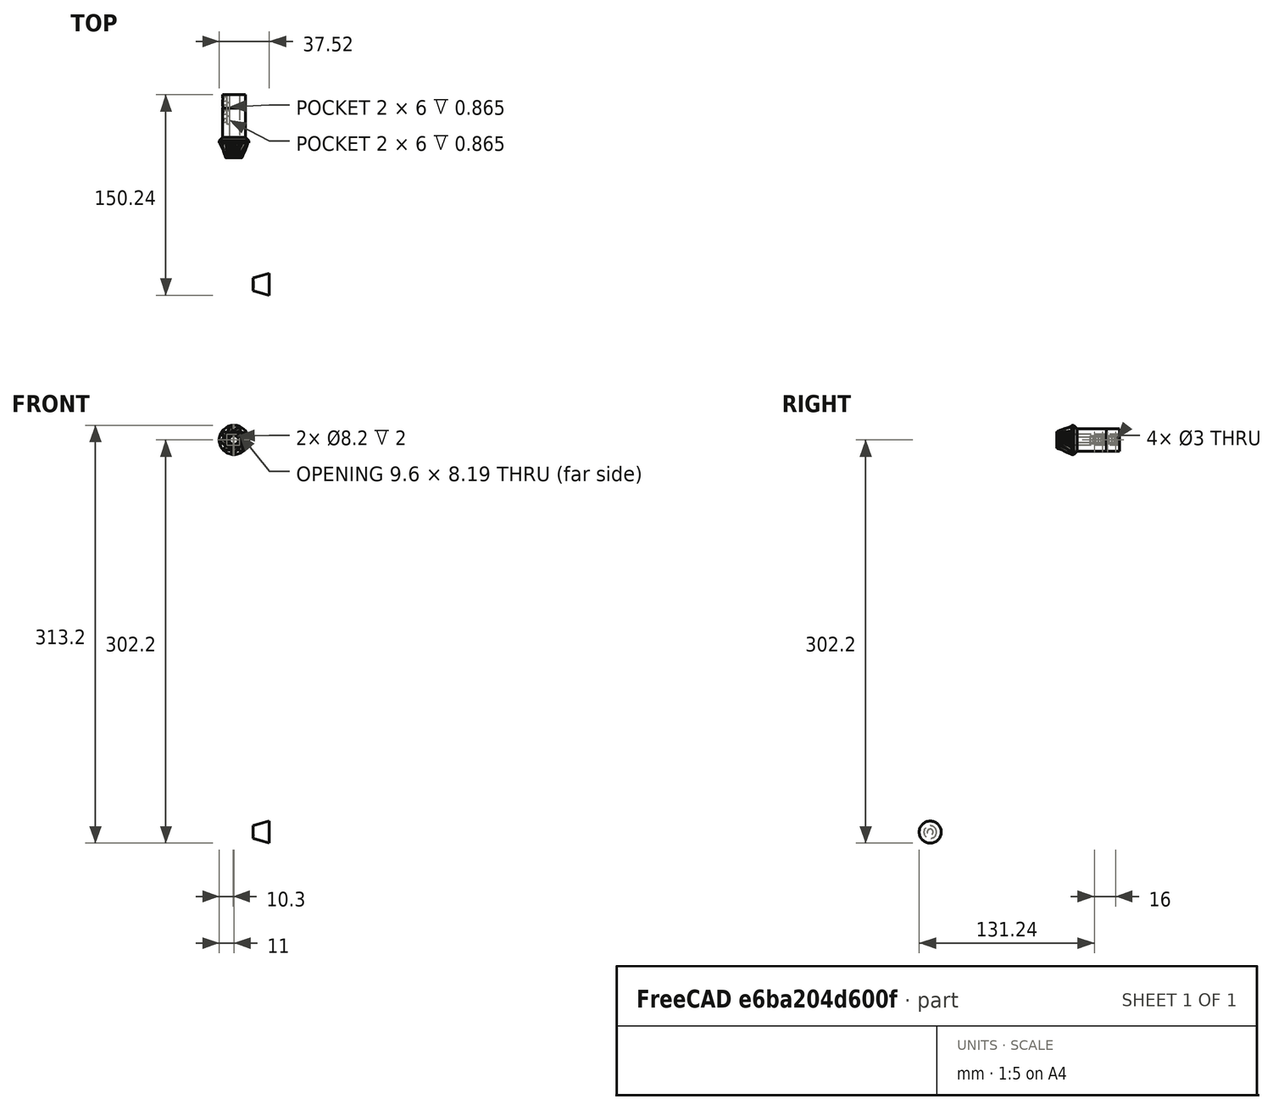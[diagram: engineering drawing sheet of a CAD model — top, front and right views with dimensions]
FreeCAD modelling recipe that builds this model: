
FCSTD DOCUMENT  (FreeCAD 0.19R24291 (Git))
Label: bazovina-prevod-C_007
License: All rights reserved
LicenseURL: http://en.wikipedia.org/wiki/All_rights_reserved
objects: Part::Cut×12, Part::Box×10, Part::Cylinder×9, Part::Compound×7, Part::FeaturePython×4, Sketcher::SketchObject×4, PartDesign::Revolution×4, PartDesign::Body×4, Part::Common×2, Part::MultiFuse×2, Mesh::Feature×2, Part::Chamfer×1
note: 63 computed .brp shape members not serialized (recipe doc carries the construction recipe); baked Part::Feature solids carry a one-line shape summary decoded from their .brp

FEATURE [Part::FeaturePython] bevelgear007  # WARN: FeaturePython — macro-defined, semantics opaque (R4)
  AttacherType = Attacher::AttachEngine3D
  Placement = pos=(26,0,-244) rot=(0,-1,0;1.5708rad)
  backlash = 0.1
  beta = 12
  clearance = 0.1
  height = 25
  module = 1.5
  numpoints = 6
  pitch_angle = 12.53
  pressure_angle = 25
  reset_origin = true
  teeth = 8
  version = 0.0.3
FEATURE [Sketcher::SketchObject] Sketch007
  FullyConstrained = false
  MapMode = 5
  Placement = pos=(0,0,0) rot=(1,0,0;1.5708rad)
  Support = -> [XZ_Plane007]
  sketch-geometry (31):
    g0: LineSegment StartX=0 StartY=-49.2912 StartZ=0 EndX=22.5 EndY=-49.2912 EndZ=0
    g1: LineSegment StartX=22.5 StartY=-49.2912 StartZ=0 EndX=22.5 EndY=-53.2912 EndZ=0
    g2: LineSegment StartX=22.5 StartY=-53.2912 StartZ=0 EndX=0 EndY=-53.2912 EndZ=0
    g3: LineSegment StartX=0 StartY=-53.2912 StartZ=0 EndX=0 EndY=-49.2912 EndZ=0
    g4: LineSegment StartX=22.5 StartY=-49.2912 StartZ=0 EndX=26.5 EndY=-49.2912 EndZ=0
    g5: LineSegment StartX=26.5 StartY=-49.2912 StartZ=0 EndX=26.5 EndY=-44.2912 EndZ=0
    g6: LineSegment StartX=26.5 StartY=-44.2912 StartZ=0 EndX=22.5 EndY=-44.2912 EndZ=0
    g7: LineSegment StartX=22.5 StartY=-44.2912 StartZ=0 EndX=22.5 EndY=-49.2912 EndZ=0
    g8: LineSegment StartX=22.5 StartY=-49.2912 StartZ=0 EndX=0 EndY=-49.2912 EndZ=0
    g9: LineSegment StartX=0 StartY=-49.2912 StartZ=0 EndX=0 EndY=-44.2912 EndZ=0
    g10: LineSegment StartX=0 StartY=-44.2912 StartZ=0 EndX=22.5 EndY=-44.2912 EndZ=0
    g11: LineSegment StartX=22.5 StartY=-44.2912 StartZ=0 EndX=22.5 EndY=-49.2912 EndZ=0
    g12: LineSegment StartX=0 StartY=-44.2912 StartZ=0 EndX=22.5 EndY=-49.2912 EndZ=0
    g13: LineSegment StartX=22.5 StartY=-49.2912 StartZ=0 EndX=22.0661 EndY=-51.2436 EndZ=0
    g14: LineSegment StartX=22.5 StartY=-49.2912 StartZ=0 EndX=22.9339 EndY=-47.3388 EndZ=0
    g15: LineSegment StartX=22.9339 StartY=-47.3388 StartZ=0 EndX=0 EndY=-44.2912 EndZ=0
    g16: LineSegment StartX=22.0661 StartY=-51.2436 StartZ=0 EndX=0 EndY=-44.2912 EndZ=0
    g17: LineSegment StartX=22.9339 StartY=-47.3388 StartZ=0 EndX=15.0036 EndY=-46.285 EndZ=0
    g18: LineSegment StartX=15.0036 StartY=-46.285 StartZ=0 EndX=14.3355 EndY=-49.2912 EndZ=0
    g19: LineSegment StartX=15.0036 StartY=-44.2912 StartZ=0 EndX=15.0036 EndY=-46.285 EndZ=0
    g20: LineSegment StartX=22.0661 StartY=-51.2436 StartZ=0 EndX=22.0661 EndY=-53.2912 EndZ=0
    g21: LineSegment StartX=22.9339 StartY=-47.3388 StartZ=0 EndX=26.5 EndY=-47.3388 EndZ=0
    g22: LineSegment StartX=15.0036 StartY=-44.2912 StartZ=0 EndX=15.0036 EndY=-46.5552 EndZ=0
    g23: LineSegment StartX=15.0036 StartY=-46.5552 StartZ=0 EndX=14.3773 EndY=-49.1034 EndZ=0
    g24: LineSegment StartX=14.3773 StartY=-49.1034 StartZ=0 EndX=22.0661 EndY=-51.2436 EndZ=0
    g25: LineSegment StartX=22.0661 StartY=-51.2436 StartZ=0 EndX=22.5 EndY=-49.2912 EndZ=0
    g26: LineSegment StartX=22.5 StartY=-49.2912 StartZ=0 EndX=26.5 EndY=-49.2912 EndZ=0
    g27: LineSegment StartX=26.5 StartY=-49.2912 StartZ=0 EndX=26.5 EndY=-44.2912 EndZ=0
    g28: LineSegment StartX=26.5 StartY=-44.2912 StartZ=0 EndX=15.0036 EndY=-44.2912 EndZ=0
    g29: LineSegment StartX=22.0661 StartY=-51.2436 StartZ=0 EndX=25.8788 EndY=-52.4534 EndZ=0
    g30: LineSegment StartX=25.8788 StartY=-52.4534 StartZ=0 EndX=26.5 EndY=-49.2912 EndZ=0
  constraints (81):
    c: Coincident(g0,g1)
    c: Coincident(g1,g2)
    c: Coincident(g2,g3)
    c: Coincident(g3,g0)
    c: Horizontal(g0)
    c: Horizontal(g2)
    c: Vertical(g1)
    c: Vertical(g3)
    c: PointOnObject(g0,g-2)
    c: Distance(g0) = 22.5
    c: Distance(g1) = 4
    c: Coincident(g4,g5)
    c: Coincident(g5,g6)
    c: Coincident(g6,g7)
    c: Coincident(g7,g4)
    c: Horizontal(g4)
    c: Horizontal(g6)
    c: Vertical(g5)
    c: Vertical(g7)
    c: Coincident(g4,g0)
    c: Distance(g7) = 5
    c: Distance(g6) = 4
    c: Coincident(g8,g9)
    c: Coincident(g9,g10)
    c: Coincident(g10,g11)
    c: Coincident(g11,g8)
    c: Horizontal(g8)
    c: Horizontal(g10)
    c: Vertical(g9)
    c: Vertical(g11)
    c: Coincident(g8,g0)
    c: PointOnObject(g9,g-2)
    c: Distance(g9) = 5
    c: Coincident(g12,g9)
    c: Coincident(g12,g0)
    c: Coincident(g13,g0)
    c: Perpendicular(g13,g12)
    c: Distance(g13) = 2
    c: Coincident(g14,g0)
    c: Distance(g14) = 2
    c: Perpendicular(g14,g12)
    c: Coincident(g15,g14)
    c: Coincident(g15,g9)
    c: Coincident(g16,g13)
    c: Coincident(g16,g9)
    c: Coincident(g17,g14)
    c: PointOnObject(g17,g15)
    c: Distance(g17) = 8
    c: Coincident(g18,g17)
    c: PointOnObject(g18,g0)
    c: Perpendicular(g18,g12)
    c: PointOnObject(g19,g10)
    c: Coincident(g19,g17)
    c: Vertical(g19)
    c: Coincident(g20,g13)
    c: PointOnObject(g20,g2)
    c: Vertical(g20)
    c: Coincident(g21,g14)
    c: PointOnObject(g21,g5)
    c: Horizontal(g21)
    c: Coincident(g19,g22)
    c: Coincident(g23,g22)
    c: PointOnObject(g23,g18)
    c: Coincident(g24,g23)
    c: Coincident(g24,g13)
    c: Coincident(g25,g24)
    c: Coincident(g25,g0)
    c: Coincident(g26,g25)
    c: Coincident(g26,g4)
    c: Coincident(g27,g26)
    c: Coincident(g27,g5)
    c: Coincident(g28,g27)
    c: Coincident(g28,g22)
    c: Vertical(g22)
    c: Angle(g15,g10) = 0.132114
    c: Angle(g12,g10) = 0.218669
    c: Angle(g9,g12) = 1.35213
    c: Coincident(g29,g24)
    c: Distance(g29) = 4
    c: Coincident(g30,g29)
    c: Coincident(g30,g26)
FEATURE [PartDesign::Revolution] Revolution007
  Angle = 360
  Axis = (22.5,0,0)
  Base = (0,9.8e-15,-44.2912)
  Placement = pos=(0,0,0) rot=(1,0,0;1.5708rad)
  Profile = -> Sketch007
  ReferenceAxis = -> Sketch007 [Axis10]
  Reversed = true
FEATURE [PartDesign::Body] Body007
  Group = -> [Sketch007,Revolution007]
  Origin = -> Origin007
  Placement = pos=(0,0,-199.6) rot=(0,0,1;0rad)
  Tip = -> Revolution007
FEATURE [Part::Common] Common009
  Base = -> Body007
  Placement = pos=(0,84,294) rot=(0,0,1;1.5708rad)
  Tool = -> bevelgear007
FEATURE [Part::Compound] Compound  label="bazovina-prevod-C1"
  Links = -> [Common009]
  Placement = pos=(0,-2,0) rot=(0,0,1;0rad)
FEATURE [Part::Box] Box247  label="Krychle247"
  AttacherType = Attacher::AttachEngine3D
  Height = 40
  Length = 40
  Placement = pos=(-20,98,30) rot=(0,0,1;0rad)
  Width = 20
FEATURE [Part::Box] Box248  label="Krychle248"
  AttacherType = Attacher::AttachEngine3D
  Height = 40
  Length = 40
  Placement = pos=(-20,88,30) rot=(0,0,1;0rad)
  Width = 20
FEATURE [Part::Box] Box249  label="Krychle249"
  AttacherType = Attacher::AttachEngine3D
  Height = 6
  Length = 6
  Placement = pos=(196.5,-3,18) rot=(0,0,1;1.5708rad)
  Width = 2
FEATURE [Part::Box] Box250  label="Krychle250"
  AttacherType = Attacher::AttachEngine3D
  Height = 6
  Length = 6
  Placement = pos=(196.5,-3,12) rot=(0,0,1;1.5708rad)
  Width = 2
FEATURE [Part::Compound] Compound027
  Links = -> [Box249,Box250]
  Placement = pos=(0,0,-20) rot=(0,0,1;0rad)
FEATURE [Part::Cylinder] Cylinder651  label="Válec651"
  Angle = 360
  AttacherType = Attacher::AttachEngine3D
  Height = 100
  Placement = pos=(100,0,21) rot=(0.57735,0.57735,0.57735;2.0944rad)
  Radius = 1.5
FEATURE [Part::Cylinder] Cylinder652  label="Válec652"
  Angle = 360
  AttacherType = Attacher::AttachEngine3D
  Height = 100
  Placement = pos=(100,0,15) rot=(0.57735,0.57735,0.57735;2.0944rad)
  Radius = 1.5
FEATURE [Part::Compound] Compound028
  Links = -> [Cylinder651,Cylinder652]
  Placement = pos=(0,0,-20) rot=(0,0,1;0rad)
FEATURE [Part::Box] Box251  label="Krychle251"
  AttacherType = Attacher::AttachEngine3D
  Height = 26
  Length = 2
  Placement = pos=(194.5,-4,4) rot=(0,0,1;0rad)
  Width = 8
FEATURE [Part::FeaturePython] Tube006  # WARN: FeaturePython — macro-defined, semantics opaque (R4)
  AttacherType = Attacher::AttachEngine3D
  Height = 32
  InnerRadius = 4.1
  OuterRadius = 8.5
  Placement = pos=(200,0,-8) rot=(0,0,1;0rad)
FEATURE [Part::MultiFuse] Fusion002
  Shapes = -> [Tube006,Box251]
FEATURE [Part::Cut] Cut257
  Base = -> Fusion002
  Tool = -> Compound027
FEATURE [Part::Cut] Cut259  label="super_spojka002"
  Base = -> Cut257
  Placement = pos=(-200,132,50) rot=(1,0,0;1.5708rad)
  Tool = -> Compound028
FEATURE [Part::Cut] Cut258
  Base = -> Cut259
  Tool = -> Box248
FEATURE [Part::Box] Box252  label="Krychle252"
  AttacherType = Attacher::AttachEngine3D
  Height = 40
  Length = 40
  Placement = pos=(-20,110,30) rot=(0,0,1;0rad)
  Width = 20
FEATURE [Part::Cut] Cut
  Base = -> Cut258
  Placement = pos=(0,-8,0) rot=(0,0,1;0rad)
  Tool = -> Box247
FEATURE [Part::Cylinder] Cylinder649  label="Válec649"
  Angle = 360
  AttacherType = Attacher::AttachEngine3D
  Height = 8
  Placement = pos=(0,114,50) rot=(1,0,0;1.5708rad)
  Radius = 8
FEATURE [Part::Cylinder] Cylinder650  label="Válec650"
  Angle = 360
  AttacherType = Attacher::AttachEngine3D
  Height = 10
  Placement = pos=(0,118,50) rot=(1,0,0;1.5708rad)
  Radius = 4.1
FEATURE [Part::Cut] Cut255
  Base = -> Cylinder649
  Tool = -> Cylinder650
FEATURE [Part::Cut] Cut260
  Base = -> Cut255
  Tool = -> Box252
FEATURE [Mesh::Feature] Mesh  label="bazovina-prevod-C002 (Meshed)"
FEATURE [Sketcher::SketchObject] Sketch008
  FullyConstrained = false
  MapMode = 5
  Placement = pos=(0,0,0) rot=(1,0,0;1.5708rad)
  Support = -> [XZ_Plane008]
  sketch-geometry (29):
    g0: LineSegment StartX=0 StartY=-49.3618 StartZ=0 EndX=22.5 EndY=-49.3618 EndZ=0
    g1: LineSegment StartX=22.5 StartY=-49.3618 StartZ=0 EndX=22.5 EndY=-53.3618 EndZ=0
    g2: LineSegment StartX=22.5 StartY=-53.3618 StartZ=0 EndX=0 EndY=-53.3618 EndZ=0
    g3: LineSegment StartX=0 StartY=-53.3618 StartZ=0 EndX=0 EndY=-49.3618 EndZ=0
    g4: LineSegment StartX=22.5 StartY=-49.3618 StartZ=0 EndX=26.5 EndY=-49.3618 EndZ=0
    g5: LineSegment StartX=26.5 StartY=-49.3618 StartZ=0 EndX=26.5 EndY=-44.3618 EndZ=0
    g6: LineSegment StartX=26.5 StartY=-44.3618 StartZ=0 EndX=22.5 EndY=-44.3618 EndZ=0
    g7: LineSegment StartX=22.5 StartY=-44.3618 StartZ=0 EndX=22.5 EndY=-49.3618 EndZ=0
    g8: LineSegment StartX=22.5 StartY=-49.3618 StartZ=0 EndX=0 EndY=-49.3618 EndZ=0
    g9: LineSegment StartX=0 StartY=-49.3618 StartZ=0 EndX=0 EndY=-44.3618 EndZ=0
    g10: LineSegment StartX=0 StartY=-44.3618 StartZ=0 EndX=22.5 EndY=-44.3618 EndZ=0
    g11: LineSegment StartX=22.5 StartY=-44.3618 StartZ=0 EndX=22.5 EndY=-49.3618 EndZ=0
    g12: LineSegment StartX=0 StartY=-44.3618 StartZ=0 EndX=22.5 EndY=-49.3618 EndZ=0
    g13: LineSegment StartX=22.5 StartY=-49.3618 StartZ=0 EndX=22.0661 EndY=-51.3142 EndZ=0
    g14: LineSegment StartX=22.5 StartY=-49.3618 StartZ=0 EndX=22.9339 EndY=-47.4094 EndZ=0
    g15: LineSegment StartX=22.9339 StartY=-47.4094 StartZ=0 EndX=0 EndY=-44.3618 EndZ=0
    g16: LineSegment StartX=22.0661 StartY=-51.3142 StartZ=0 EndX=0 EndY=-44.3618 EndZ=0
    g17: LineSegment StartX=22.9339 StartY=-47.4094 StartZ=0 EndX=15.0036 EndY=-46.3556 EndZ=0
    g18: LineSegment StartX=15.0036 StartY=-46.3556 StartZ=0 EndX=14.3355 EndY=-49.3618 EndZ=0
    g19: LineSegment StartX=15.0036 StartY=-44.3618 StartZ=0 EndX=15.0036 EndY=-46.3556 EndZ=0
    g20: LineSegment StartX=22.0661 StartY=-51.3142 StartZ=0 EndX=22.0661 EndY=-53.3618 EndZ=0
    g21: LineSegment StartX=22.9339 StartY=-47.4094 StartZ=0 EndX=26.5 EndY=-47.4094 EndZ=0
    g22: LineSegment StartX=15.0036 StartY=-44.3618 StartZ=0 EndX=15.0036 EndY=-46.5552 EndZ=0
    g23: LineSegment StartX=15.0036 StartY=-46.5552 StartZ=0 EndX=14.3934 EndY=-49.1013 EndZ=0
    g24: LineSegment StartX=14.3934 StartY=-49.1013 StartZ=0 EndX=22.0661 EndY=-51.3142 EndZ=0
    g25: LineSegment StartX=26.5232 StartY=-49.2912 StartZ=0 EndX=26.5 EndY=-44.3618 EndZ=0
    g26: LineSegment StartX=26.5 StartY=-44.3618 StartZ=0 EndX=15.0036 EndY=-44.3618 EndZ=0
    g27: LineSegment StartX=26.5232 StartY=-49.2912 StartZ=0 EndX=26.5232 EndY=-52.5996 EndZ=0
    g28: LineSegment StartX=22.0661 StartY=-51.3142 StartZ=0 EndX=26.5232 EndY=-52.5996 EndZ=0
  constraints (77):
    c: Coincident(g0,g1)
    c: Coincident(g1,g2)
    c: Coincident(g2,g3)
    c: Coincident(g3,g0)
    c: Horizontal(g0)
    c: Horizontal(g2)
    c: Vertical(g1)
    c: Vertical(g3)
    c: PointOnObject(g0,g-2)
    c: Distance(g0) = 22.5
    c: Distance(g1) = 4
    c: Coincident(g4,g5)
    c: Coincident(g5,g6)
    c: Coincident(g6,g7)
    c: Coincident(g7,g4)
    c: Horizontal(g4)
    c: Horizontal(g6)
    c: Vertical(g5)
    c: Vertical(g7)
    c: Coincident(g4,g0)
    c: Distance(g7) = 5
    c: Distance(g6) = 4
    c: Coincident(g8,g9)
    c: Coincident(g9,g10)
    c: Coincident(g10,g11)
    c: Coincident(g11,g8)
    c: Horizontal(g8)
    c: Horizontal(g10)
    c: Vertical(g9)
    c: Vertical(g11)
    c: Coincident(g8,g0)
    c: PointOnObject(g9,g-2)
    c: Distance(g9) = 5
    c: Coincident(g12,g9)
    c: Coincident(g12,g0)
    c: Coincident(g13,g0)
    c: Perpendicular(g13,g12)
    c: Distance(g13) = 2
    c: Coincident(g14,g0)
    c: Distance(g14) = 2
    c: Perpendicular(g14,g12)
    c: Coincident(g15,g14)
    c: Coincident(g15,g9)
    c: Coincident(g16,g13)
    c: Coincident(g16,g9)
    c: Coincident(g17,g14)
    c: PointOnObject(g17,g15)
    c: Distance(g17) = 8
    c: Coincident(g18,g17)
    c: PointOnObject(g18,g0)
    c: Perpendicular(g18,g12)
    c: PointOnObject(g19,g10)
    c: Coincident(g19,g17)
    c: Vertical(g19)
    c: Coincident(g20,g13)
    c: PointOnObject(g20,g2)
    c: Vertical(g20)
    c: Coincident(g21,g14)
    c: PointOnObject(g21,g5)
    c: Horizontal(g21)
    c: Coincident(g19,g22)
    c: Coincident(g23,g22)
    c: PointOnObject(g23,g18)
    c: Coincident(g24,g23)
    c: Coincident(g24,g13)
    c: Coincident(g25,g5)
    c: Coincident(g26,g25)
    c: Coincident(g26,g22)
    c: Vertical(g22)
    c: Angle(g15,g10) = 0.132114
    c: Angle(g12,g10) = 0.218669
    c: Angle(g9,g12) = 1.35213
    c: Coincident(g27,g25)
    c: Vertical(g27)
    c: Coincident(g28,g24)
    c: Coincident(g28,g27)
    c: Parallel(g24,g28)
FEATURE [PartDesign::Revolution] Revolution008
  Angle = 360
  Axis = (22.5,0,0)
  Base = (0,9.9e-15,-44.3618)
  Placement = pos=(0,0,0) rot=(1,0,0;1.5708rad)
  Profile = -> Sketch008
  ReferenceAxis = -> Sketch008 [Axis10]
  Reversed = true
FEATURE [PartDesign::Body] Body008
  Group = -> [Sketch008,Revolution008]
  Origin = -> Origin008
  Placement = pos=(0,0,-199.6) rot=(0,0,1;0rad)
  Tip = -> Revolution008
FEATURE [Part::Cylinder] Cylinder653  label="Válec653"
  Angle = 360
  AttacherType = Attacher::AttachEngine3D
  Height = 8
  Placement = pos=(0,98,50) rot=(1,0,0;1.5708rad)
  Radius = 7
FEATURE [Part::Cut] Cut261
  Base = -> Compound
  Tool = -> Cylinder653
FEATURE [Part::Compound] Compound029  label="bazovina-prevod-C"
  Links = -> [Cut,Cut260,Cut261]
FEATURE [Mesh::Feature] Mesh001  label="bazovina-prevod-C (Meshed)"
FEATURE [Sketcher::SketchObject] Sketch012
  FullyConstrained = false
  MapMode = 5
  Placement = pos=(0,0,0) rot=(1,0,0;1.5708rad)
  Support = -> [XZ_Plane012]
  sketch-geometry (29):
    g0: LineSegment StartX=0 StartY=-49.6356 StartZ=0 EndX=22.5 EndY=-49.6356 EndZ=0
    g1: LineSegment StartX=22.5 StartY=-49.6356 StartZ=0 EndX=22.5 EndY=-53.6356 EndZ=0
    g2: LineSegment StartX=22.5 StartY=-53.6356 StartZ=0 EndX=0 EndY=-53.6356 EndZ=0
    g3: LineSegment StartX=0 StartY=-53.6356 StartZ=0 EndX=0 EndY=-49.6356 EndZ=0
    g4: LineSegment StartX=22.5 StartY=-49.6356 StartZ=0 EndX=26.5 EndY=-49.6356 EndZ=0
    g5: LineSegment StartX=26.5 StartY=-49.6356 StartZ=0 EndX=26.5 EndY=-42.6356 EndZ=0
    g6: LineSegment StartX=26.5 StartY=-42.6356 StartZ=0 EndX=22.5 EndY=-42.6356 EndZ=0
    g7: LineSegment StartX=22.5 StartY=-42.6356 StartZ=0 EndX=22.5 EndY=-49.6356 EndZ=0
    g8: LineSegment StartX=22.5 StartY=-49.6356 StartZ=0 EndX=0 EndY=-49.6356 EndZ=0
    g9: LineSegment StartX=0 StartY=-49.6356 StartZ=0 EndX=0 EndY=-42.6356 EndZ=0
    g10: LineSegment StartX=0 StartY=-42.6356 StartZ=0 EndX=22.5 EndY=-42.6356 EndZ=0
    g11: LineSegment StartX=22.5 StartY=-42.6356 StartZ=0 EndX=22.5 EndY=-49.6356 EndZ=0
    g12: LineSegment StartX=0 StartY=-42.6356 StartZ=0 EndX=22.5 EndY=-49.6356 EndZ=0
    g13: LineSegment StartX=22.5 StartY=-49.6356 StartZ=0 EndX=21.9059 EndY=-51.5453 EndZ=0
    g14: LineSegment StartX=22.5 StartY=-49.6356 StartZ=0 EndX=23.0941 EndY=-47.7259 EndZ=0
    g15: LineSegment StartX=23.0941 StartY=-47.7259 StartZ=0 EndX=0 EndY=-42.6356 EndZ=0
    g16: LineSegment StartX=21.9059 StartY=-51.5453 StartZ=0 EndX=0 EndY=-42.6356 EndZ=0
    g17: LineSegment StartX=23.0941 StartY=-47.7259 StartZ=0 EndX=15.2817 EndY=-46.0039 EndZ=0
    g18: LineSegment StartX=15.2817 StartY=-46.0039 StartZ=0 EndX=14.1518 EndY=-49.6356 EndZ=0
    g19: LineSegment StartX=15.2817 StartY=-42.6356 StartZ=0 EndX=15.2817 EndY=-46.0039 EndZ=0
    g20: LineSegment StartX=21.9059 StartY=-51.5453 StartZ=0 EndX=21.9059 EndY=-53.6356 EndZ=0
    g21: LineSegment StartX=23.0941 StartY=-47.7259 StartZ=0 EndX=26.5 EndY=-47.7259 EndZ=0
    g22: LineSegment StartX=15.2817 StartY=-42.6356 StartZ=0 EndX=15.2817 EndY=-46.5709 EndZ=0
    g23: LineSegment StartX=15.2817 StartY=-46.5709 StartZ=0 EndX=14.4998 EndY=-48.5171 EndZ=0
    g24: LineSegment StartX=14.4998 StartY=-48.5171 StartZ=0 EndX=21.9059 EndY=-51.5453 EndZ=0
    g25: LineSegment StartX=26.275 StartY=-49.2912 StartZ=0 EndX=26.5 EndY=-42.6356 EndZ=0
    g26: LineSegment StartX=26.5 StartY=-42.6356 StartZ=0 EndX=15.2817 EndY=-42.6356 EndZ=0
    g27: LineSegment StartX=26.275 StartY=-49.2912 StartZ=0 EndX=26.275 EndY=-53.3318 EndZ=0
    g28: LineSegment StartX=21.9059 StartY=-51.5453 StartZ=0 EndX=26.275 EndY=-53.3318 EndZ=0
  constraints (77):
    c: Coincident(g0,g1)
    c: Coincident(g1,g2)
    c: Coincident(g2,g3)
    c: Coincident(g3,g0)
    c: Horizontal(g0)
    c: Horizontal(g2)
    c: Vertical(g1)
    c: Vertical(g3)
    c: PointOnObject(g0,g-2)
    c: Distance(g0) = 22.5
    c: Distance(g1) = 4
    c: Coincident(g4,g5)
    c: Coincident(g5,g6)
    c: Coincident(g6,g7)
    c: Coincident(g7,g4)
    c: Horizontal(g4)
    c: Horizontal(g6)
    c: Vertical(g5)
    c: Vertical(g7)
    c: Coincident(g4,g0)
    c: Distance(g7) = 7
    c: Distance(g6) = 4
    c: Coincident(g8,g9)
    c: Coincident(g9,g10)
    c: Coincident(g10,g11)
    c: Coincident(g11,g8)
    c: Horizontal(g8)
    c: Horizontal(g10)
    c: Vertical(g9)
    c: Vertical(g11)
    c: Coincident(g8,g0)
    c: PointOnObject(g9,g-2)
    c: Distance(g9) = 7
    c: Coincident(g12,g9)
    c: Coincident(g12,g0)
    c: Coincident(g13,g0)
    c: Perpendicular(g13,g12)
    c: Distance(g13) = 2
    c: Coincident(g14,g0)
    c: Distance(g14) = 2
    c: Perpendicular(g14,g12)
    c: Coincident(g15,g14)
    c: Coincident(g15,g9)
    c: Coincident(g16,g13)
    c: Coincident(g16,g9)
    c: Coincident(g17,g14)
    c: PointOnObject(g17,g15)
    c: Distance(g17) = 8
    c: Coincident(g18,g17)
    c: PointOnObject(g18,g0)
    c: Perpendicular(g18,g12)
    c: PointOnObject(g19,g10)
    c: Coincident(g19,g17)
    c: Vertical(g19)
    c: Coincident(g20,g13)
    c: PointOnObject(g20,g2)
    c: Vertical(g20)
    c: Coincident(g21,g14)
    c: PointOnObject(g21,g5)
    c: Horizontal(g21)
    c: Coincident(g19,g22)
    c: Coincident(g23,g22)
    c: PointOnObject(g23,g18)
    c: Coincident(g24,g23)
    c: Coincident(g24,g13)
    c: Coincident(g25,g5)
    c: Coincident(g26,g25)
    c: Coincident(g26,g22)
    c: Vertical(g22)
    c: Angle(g15,g10) = 0.216946
    c: Angle(g12,g10) = 0.301619
    c: Angle(g9,g12) = 1.26918
    c: Coincident(g27,g25)
    c: Vertical(g27)
    c: Coincident(g28,g24)
    c: Coincident(g28,g27)
    c: Parallel(g24,g28)
FEATURE [PartDesign::Revolution] Revolution012
  Angle = 360
  Axis = (22.5,0,0)
  Base = (0,9.5e-15,-42.6356)
  Placement = pos=(0,0,0) rot=(1,0,0;1.5708rad)
  Profile = -> Sketch012
  ReferenceAxis = -> Sketch012 [Axis10]
  Reversed = true
FEATURE [PartDesign::Body] Body010
  Group = -> [Revolution012,Sketch012]
  Origin = -> Origin010
  Placement = pos=(-12.5,0,-201.4) rot=(0,0,1;0rad)
  Tip = -> Revolution012
FEATURE [Part::FeaturePython] bevelgear008  # WARN: FeaturePython — macro-defined, semantics opaque (R4)
  AttacherType = Attacher::AttachEngine3D
  Placement = pos=(26,0,-244) rot=(0,-1,0;1.5708rad)
  backlash = 0.1
  beta = 12
  clearance = 0.1
  height = 30
  module = 2
  numpoints = 6
  pitch_angle = 17.29
  pressure_angle = 25
  reset_origin = true
  teeth = 9
  version = 0.0.3
FEATURE [Sketcher::SketchObject] Sketch011
  FullyConstrained = false
  MapMode = 5
  Placement = pos=(0,0,0) rot=(1,0,0;1.5708rad)
  Support = -> [XZ_Plane013]
  sketch-geometry (29):
    g0: LineSegment StartX=0 StartY=-49.6356 StartZ=0 EndX=22.5 EndY=-49.6356 EndZ=0
    g1: LineSegment StartX=22.5 StartY=-49.6356 StartZ=0 EndX=22.5 EndY=-53.6356 EndZ=0
    g2: LineSegment StartX=22.5 StartY=-53.6356 StartZ=0 EndX=0 EndY=-53.6356 EndZ=0
    g3: LineSegment StartX=0 StartY=-53.6356 StartZ=0 EndX=0 EndY=-49.6356 EndZ=0
    g4: LineSegment StartX=22.5 StartY=-49.6356 StartZ=0 EndX=26.5 EndY=-49.6356 EndZ=0
    g5: LineSegment StartX=26.5 StartY=-49.6356 StartZ=0 EndX=26.5 EndY=-42.6356 EndZ=0
    g6: LineSegment StartX=26.5 StartY=-42.6356 StartZ=0 EndX=22.5 EndY=-42.6356 EndZ=0
    g7: LineSegment StartX=22.5 StartY=-42.6356 StartZ=0 EndX=22.5 EndY=-49.6356 EndZ=0
    g8: LineSegment StartX=22.5 StartY=-49.6356 StartZ=0 EndX=0 EndY=-49.6356 EndZ=0
    g9: LineSegment StartX=0 StartY=-49.6356 StartZ=0 EndX=0 EndY=-42.6356 EndZ=0
    g10: LineSegment StartX=0 StartY=-42.6356 StartZ=0 EndX=22.5 EndY=-42.6356 EndZ=0
    g11: LineSegment StartX=22.5 StartY=-42.6356 StartZ=0 EndX=22.5 EndY=-49.6356 EndZ=0
    g12: LineSegment StartX=0 StartY=-42.6356 StartZ=0 EndX=22.5 EndY=-49.6356 EndZ=0
    g13: LineSegment StartX=22.5 StartY=-49.6356 StartZ=0 EndX=21.9059 EndY=-51.5453 EndZ=0
    g14: LineSegment StartX=22.5 StartY=-49.6356 StartZ=0 EndX=23.0941 EndY=-47.7259 EndZ=0
    g15: LineSegment StartX=23.0941 StartY=-47.7259 StartZ=0 EndX=0 EndY=-42.6356 EndZ=0
    g16: LineSegment StartX=21.9059 StartY=-51.5453 StartZ=0 EndX=0 EndY=-42.6356 EndZ=0
    g17: LineSegment StartX=23.0941 StartY=-47.7259 StartZ=0 EndX=15.2817 EndY=-46.0039 EndZ=0
    g18: LineSegment StartX=15.2817 StartY=-46.0039 StartZ=0 EndX=14.1518 EndY=-49.6356 EndZ=0
    g19: LineSegment StartX=15.2817 StartY=-42.6356 StartZ=0 EndX=15.2817 EndY=-46.0039 EndZ=0
    g20: LineSegment StartX=21.9059 StartY=-51.5453 StartZ=0 EndX=21.9059 EndY=-53.6356 EndZ=0
    g21: LineSegment StartX=23.0941 StartY=-47.7259 StartZ=0 EndX=26.5 EndY=-47.7259 EndZ=0
    g22: LineSegment StartX=15.2817 StartY=-42.6356 StartZ=0 EndX=15.2817 EndY=-46.5709 EndZ=0
    g23: LineSegment StartX=15.2817 StartY=-46.5709 StartZ=0 EndX=14.4998 EndY=-48.5171 EndZ=0
    g24: LineSegment StartX=14.4998 StartY=-48.5171 StartZ=0 EndX=21.9059 EndY=-51.5453 EndZ=0
    g25: LineSegment StartX=26.275 StartY=-49.2912 StartZ=0 EndX=26.5 EndY=-42.6356 EndZ=0
    g26: LineSegment StartX=26.5 StartY=-42.6356 StartZ=0 EndX=15.2817 EndY=-42.6356 EndZ=0
    g27: LineSegment StartX=26.275 StartY=-49.2912 StartZ=0 EndX=26.275 EndY=-53.3318 EndZ=0
    g28: LineSegment StartX=21.9059 StartY=-51.5453 StartZ=0 EndX=26.275 EndY=-53.3318 EndZ=0
  constraints (77):
    c: Coincident(g0,g1)
    c: Coincident(g1,g2)
    c: Coincident(g2,g3)
    c: Coincident(g3,g0)
    c: Horizontal(g0)
    c: Horizontal(g2)
    c: Vertical(g1)
    c: Vertical(g3)
    c: PointOnObject(g0,g-2)
    c: Distance(g0) = 22.5
    c: Distance(g1) = 4
    c: Coincident(g4,g5)
    c: Coincident(g5,g6)
    c: Coincident(g6,g7)
    c: Coincident(g7,g4)
    c: Horizontal(g4)
    c: Horizontal(g6)
    c: Vertical(g5)
    c: Vertical(g7)
    c: Coincident(g4,g0)
    c: Distance(g7) = 7
    c: Distance(g6) = 4
    c: Coincident(g8,g9)
    c: Coincident(g9,g10)
    c: Coincident(g10,g11)
    c: Coincident(g11,g8)
    c: Horizontal(g8)
    c: Horizontal(g10)
    c: Vertical(g9)
    c: Vertical(g11)
    c: Coincident(g8,g0)
    c: PointOnObject(g9,g-2)
    c: Distance(g9) = 7
    c: Coincident(g12,g9)
    c: Coincident(g12,g0)
    c: Coincident(g13,g0)
    c: Perpendicular(g13,g12)
    c: Distance(g13) = 2
    c: Coincident(g14,g0)
    c: Distance(g14) = 2
    c: Perpendicular(g14,g12)
    c: Coincident(g15,g14)
    c: Coincident(g15,g9)
    c: Coincident(g16,g13)
    c: Coincident(g16,g9)
    c: Coincident(g17,g14)
    c: PointOnObject(g17,g15)
    c: Distance(g17) = 8
    c: Coincident(g18,g17)
    c: PointOnObject(g18,g0)
    c: Perpendicular(g18,g12)
    c: PointOnObject(g19,g10)
    c: Coincident(g19,g17)
    c: Vertical(g19)
    c: Coincident(g20,g13)
    c: PointOnObject(g20,g2)
    c: Vertical(g20)
    c: Coincident(g21,g14)
    c: PointOnObject(g21,g5)
    c: Horizontal(g21)
    c: Coincident(g19,g22)
    c: Coincident(g23,g22)
    c: PointOnObject(g23,g18)
    c: Coincident(g24,g23)
    c: Coincident(g24,g13)
    c: Coincident(g25,g5)
    c: Coincident(g26,g25)
    c: Coincident(g26,g22)
    c: Vertical(g22)
    c: Angle(g15,g10) = 0.216946
    c: Angle(g12,g10) = 0.301619
    c: Angle(g9,g12) = 1.26918
    c: Coincident(g27,g25)
    c: Vertical(g27)
    c: Coincident(g28,g24)
    c: Coincident(g28,g27)
    c: Parallel(g24,g28)
FEATURE [PartDesign::Revolution] Revolution011
  Angle = 360
  Axis = (22.5,0,0)
  Base = (0,9.5e-15,-42.6356)
  Placement = pos=(0,0,0) rot=(1,0,0;1.5708rad)
  Profile = -> Sketch011
  ReferenceAxis = -> Sketch011 [Axis10]
  Reversed = true
FEATURE [PartDesign::Body] Body009
  Group = -> [Revolution011,Sketch011]
  Origin = -> Origin009
  Placement = pos=(-1.4,0,-201.4) rot=(0,0,1;0rad)
  Tip = -> Revolution011
FEATURE [Part::Common] Common
  Base = -> bevelgear008
  Tool = -> Body009
FEATURE [Part::Cut] Cut262
  Base = -> Common
  Placement = pos=(0,81,294) rot=(0,0,1;1.5708rad)
  Tool = -> Body010
FEATURE [Part::Cylinder] Cylinder654  label="Válec654"
  Angle = 360
  AttacherType = Attacher::AttachEngine3D
  Height = 100
  Placement = pos=(100,0,21) rot=(0.57735,0.57735,0.57735;2.0944rad)
  Radius = 1.5
FEATURE [Part::Box] Box254  label="Krychle254"
  AttacherType = Attacher::AttachEngine3D
  Height = 6
  Length = 6
  Placement = pos=(196.5,-3,12) rot=(0,0,1;1.5708rad)
  Width = 2
FEATURE [Part::Cylinder] Cylinder655  label="Válec655"
  Angle = 360
  AttacherType = Attacher::AttachEngine3D
  Height = 100
  Placement = pos=(100,0,15) rot=(0.57735,0.57735,0.57735;2.0944rad)
  Radius = 1.5
FEATURE [Part::Compound] Compound031
  Links = -> [Cylinder654,Cylinder655]
  Placement = pos=(0,0,-20) rot=(0,0,1;0rad)
FEATURE [Part::Box] Box255  label="Krychle255"
  AttacherType = Attacher::AttachEngine3D
  Height = 6
  Length = 6
  Placement = pos=(196.5,-3,18) rot=(0,0,1;1.5708rad)
  Width = 2
FEATURE [Part::Compound] Compound030
  Links = -> [Box255,Box254]
  Placement = pos=(0,0,-20) rot=(0,0,1;0rad)
FEATURE [Part::FeaturePython] Tube007  # WARN: FeaturePython — macro-defined, semantics opaque (R4)
  AttacherType = Attacher::AttachEngine3D
  Height = 32
  InnerRadius = 4.1
  OuterRadius = 8.5
  Placement = pos=(200,0,-8) rot=(0,0,1;0rad)
FEATURE [Part::Cylinder] Cylinder656  label="Válec656"
  Angle = 360
  AttacherType = Attacher::AttachEngine3D
  Height = 10
  Placement = pos=(0,118,50) rot=(1,0,0;1.5708rad)
  Radius = 4.1
FEATURE [Part::Box] Box256  label="Krychle256"
  AttacherType = Attacher::AttachEngine3D
  Height = 40
  Length = 40
  Placement = pos=(-20,110,30) rot=(0,0,1;0rad)
  Width = 20
FEATURE [Part::Cylinder] Cylinder657  label="Válec657"
  Angle = 360
  AttacherType = Attacher::AttachEngine3D
  Height = 4
  Placement = pos=(0,110,50) rot=(1,0,0;1.5708rad)
  Radius = 11
FEATURE [Part::Cut] Cut265
  Base = -> Cylinder657
  Tool = -> Cylinder656
FEATURE [Part::Cut] Cut266
  Base = -> Cut265
  Tool = -> Box256
FEATURE [Part::Box] Box253  label="Krychle253"
  AttacherType = Attacher::AttachEngine3D
  Height = 24
  Length = 2
  Placement = pos=(194.5,-4,4) rot=(0,0,1;0rad)
  Width = 8
FEATURE [Part::MultiFuse] Fusion003
  Shapes = -> [Tube007,Box253]
FEATURE [Part::Cut] Cut263
  Base = -> Fusion003
  Tool = -> Compound030
FEATURE [Part::Cut] Cut264  label="super_spojka003"
  Base = -> Cut263
  Placement = pos=(-200,134,50) rot=(1,0,0;1.5708rad)
  Tool = -> Compound031
FEATURE [Part::Chamfer] Chamfer
  Base = -> Cut266
  Edges = 1 edges r=2.5: [Edge3]
FEATURE [Part::Compound] Compound032  label="Base_rear-gear-small"
  Links = -> [Cut262,Cut264,Chamfer]
